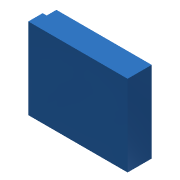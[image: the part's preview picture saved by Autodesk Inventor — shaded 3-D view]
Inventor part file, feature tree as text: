
AUTODESK INVENTOR PART (.ipt)
format: ipt  version: 2014 (Build 180170000, 170)  size: 93,184 bytes
history: native  units: in
note: dims shown in document units (in); Inventor stores cm internally (conversion verified against a paired STEP export)
features: extrude x2, sketch x2, other x2, plane x1
ambient origin geometry x8: Origin, YZ Plane, XZ Plane, XY Plane, X Axis, Y Axis, Z Axis, Center Point
bodies: Solid1 (feature_tree)
feature tree (7):
  extrude  "Extrusion1"  Depth=0.44in
  sketch  "Sketch2"  dims[d2=0.156in d3=0.0in d4=0.075in d5=0.2in d6=0.0in]
  plane  "Work Plane1"
  extrude  "Extrusion2"  Depth=0.075in
  other  "Move Face1"
  other  "Move Face2"
  sketch  "Sketch1"  dims[d0=0.498in d1=0.44in]
